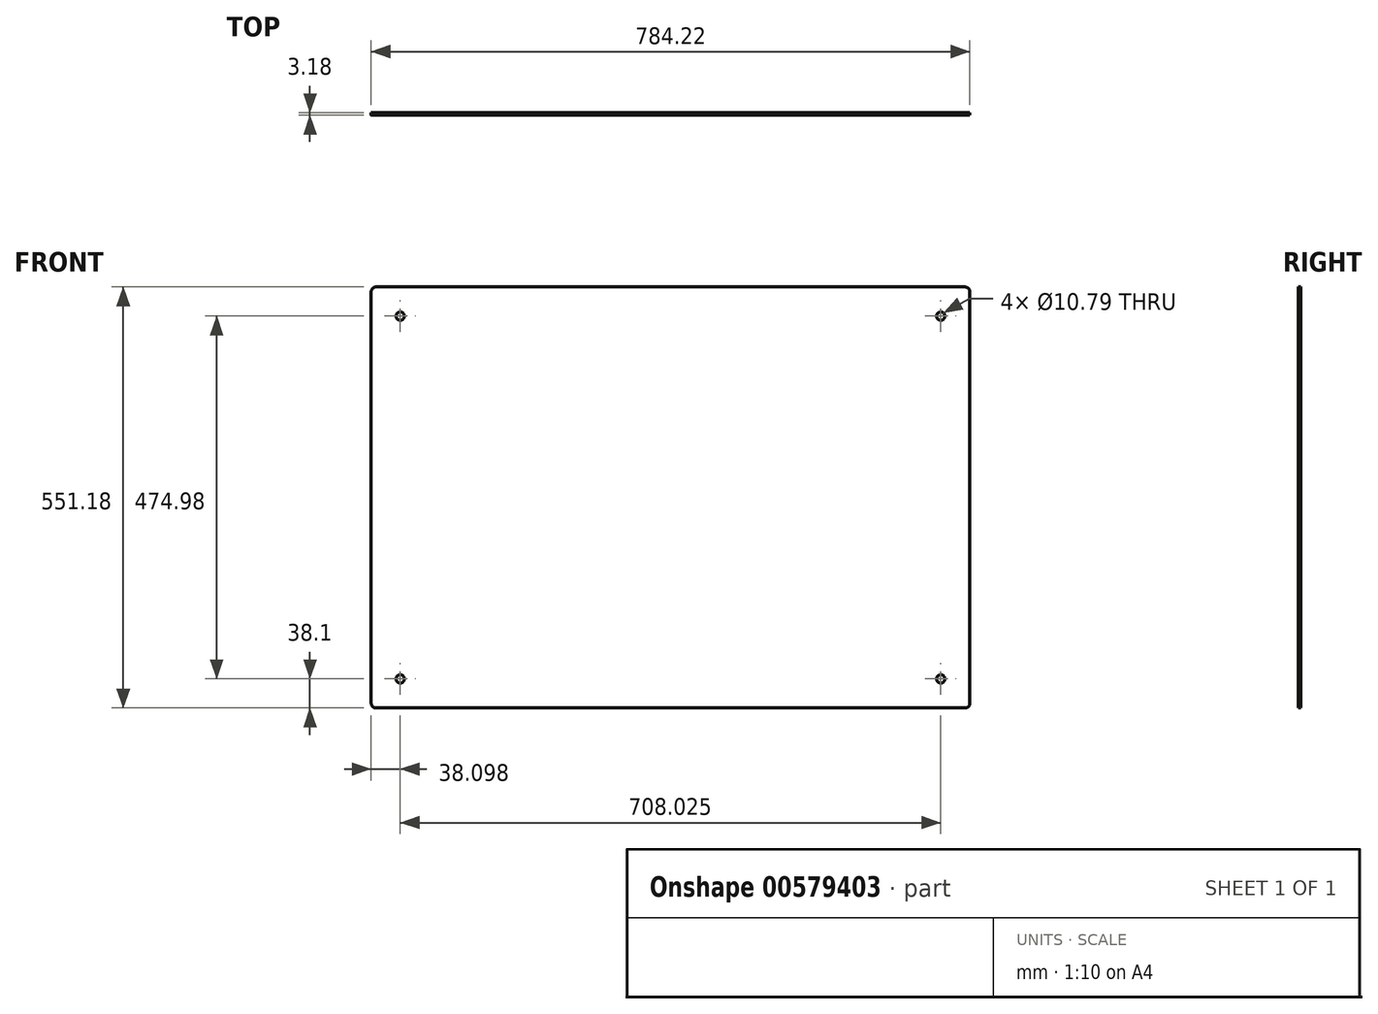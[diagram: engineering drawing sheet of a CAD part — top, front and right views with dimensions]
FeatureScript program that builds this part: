
annotation { "Feature Type Name" : "Feature", "Feature Type Description" : "" }
export const myFeature = defineFeature(function(context is Context, id is Id, definition is map)
    precondition{}
    {
        {
            var Q0;
            Q0=qCreatedBy(makeId("Front.planeOp"),FACE);
            var sketch = newSketch(context, id + "F0", { "sketchPlane" : qUnion([Q0])});
            skLineSegment(sketch, "E0.bottom", {"start": v(385.76, -275.59) * mm, "end": v(-385.76, -275.59) * mm});
            skLineSegment(sketch, "E0.top", {"start": v(385.76, 275.59) * mm, "end": v(-385.76, 275.59) * mm});
            skLineSegment(sketch, "E0.left", {"start": v(392.11, -269.24) * mm, "end": v(392.11, 269.24) * mm});
            skLineSegment(sketch, "E0.right", {"start": v(-392.11, -269.24) * mm, "end": v(-392.11, 269.24) * mm});
            skPoint(sketch, "E0.middle", {"position": v(0, 0) * mm});
            skLineSegment(sketch, "E1.bottom", {"start": v(354.01, -237.49) * mm, "end": v(-354.01, -237.49) * mm, "construction": true});
            skLineSegment(sketch, "E1.top", {"start": v(354.01, 237.5) * mm, "end": v(-354.01, 237.5) * mm, "construction": true});
            skLineSegment(sketch, "E1.left", {"start": v(354.01, -237.49) * mm, "end": v(354.01, 237.5) * mm, "construction": true});
            skLineSegment(sketch, "E1.right", {"start": v(-354.01, -237.49) * mm, "end": v(-354.01, 237.5) * mm, "construction": true});
            skCircle(sketch, "E2", {"center": v(-354.01, 237.5) * mm, "radius": 5.4 * mm});
            skCircle(sketch, "E3", {"center": v(354.01, 237.5) * mm, "radius": 5.4 * mm});
            skCircle(sketch, "E4", {"center": v(354.01, -237.49) * mm, "radius": 5.4 * mm});
            skCircle(sketch, "E5", {"center": v(-354.01, -237.49) * mm, "radius": 5.4 * mm});
            skPoint(sketch, "E6.visualSharp", {"position": v(-392.11, 275.59) * mm});
            skArc(sketch, "E6.filletArc", {"start": v(-385.76, 275.59) * mm, "mid": v(-390.25, 273.73) * mm, "end": v(-392.11, 269.24) * mm});
            skPoint(sketch, "E7.visualSharp", {"position": v(392.11, 275.59) * mm});
            skArc(sketch, "E7.filletArc", {"start": v(392.11, 269.24) * mm, "mid": v(390.25, 273.73) * mm, "end": v(385.76, 275.6) * mm});
            skPoint(sketch, "E8.visualSharp", {"position": v(392.11, -275.59) * mm});
            skArc(sketch, "E8.filletArc", {"start": v(385.76, -275.59) * mm, "mid": v(390.25, -273.73) * mm, "end": v(392.11, -269.24) * mm});
            skPoint(sketch, "E9.visualSharp", {"position": v(-392.11, -275.59) * mm});
            skArc(sketch, "E9.filletArc", {"start": v(-392.11, -269.24) * mm, "mid": v(-390.25, -273.73) * mm, "end": v(-385.76, -275.59) * mm});
            skSolve(sketch);
        }
        {
            var Q0;
            Q0=makeQuery(id+"F0.imprint","IMPRINT",FACE,{"disambiguationData":[TD([[makeQuery(id+"F0.imprint","IMPRINT",EDGE,{"derivedFrom":sQuery(id+"F0.wireOp",EDGE,"E0.bottom")}),-1.0]])]});
            extrude(context, id + "F1", {"entities" : qUnion([Q0]), "depth" : 3.17 * mm, "offsetDistance" : 25.4 * mm});
        }
    });
